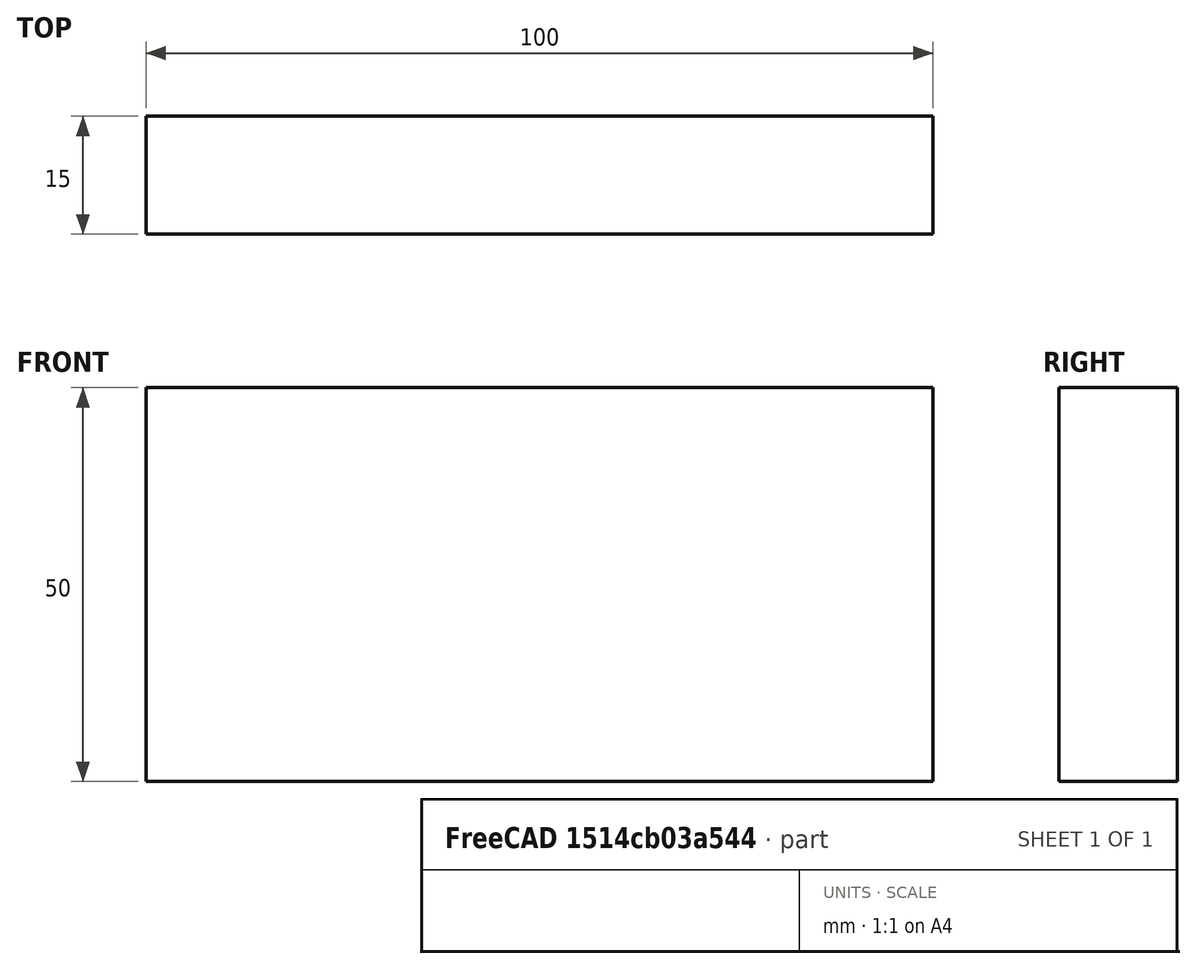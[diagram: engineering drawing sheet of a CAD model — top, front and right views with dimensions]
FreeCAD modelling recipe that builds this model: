
FCSTD DOCUMENT  (FreeCAD 0.15R4671 (Git))
Label: Flat Bar 100x15 EN10058 S235JR
License: All rights reserved
LicenseURL: http://en.wikipedia.org/wiki/All_rights_reserved
objects: Sketcher::SketchObject×1, Part::Extrusion×1
note: 2 computed .brp shape members not serialized (recipe doc carries the construction recipe); baked Part::Feature solids carry a one-line shape summary decoded from their .brp

FEATURE [Sketcher::SketchObject] Sketch
  sketch-geometry (4):
    g0: LineSegment StartX=-50 StartY=-7.5 StartZ=0 EndX=50 EndY=-7.5 EndZ=0
    g1: LineSegment StartX=50 StartY=-7.5 StartZ=0 EndX=50 EndY=7.5 EndZ=0
    g2: LineSegment StartX=50 StartY=7.5 StartZ=0 EndX=-50 EndY=7.5 EndZ=0
    g3: LineSegment StartX=-50 StartY=7.5 StartZ=0 EndX=-50 EndY=-7.5 EndZ=0
  constraints (12):
    c: Coincident(g0,g1)
    c: Coincident(g1,g2)
    c: Coincident(g2,g3)
    c: Coincident(g3,g0)
    c: Horizontal(g0)
    c: Horizontal(g2)
    c: Vertical(g1)
    c: Vertical(g3)
    c: Symmetric(g1,g2,g-2)
    c: Symmetric(g0,g1,g-1)
    c: DistanceY(g1) = 15
    c: DistanceX(g0) = 100
FEATURE [Part::Extrusion] Extrude  label="Flat Bar 100x15 EN10058 S235JR"
  Base = -> Sketch
  Dir = (0,0,50)
  Solid = true
